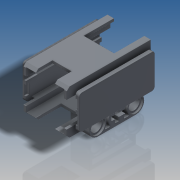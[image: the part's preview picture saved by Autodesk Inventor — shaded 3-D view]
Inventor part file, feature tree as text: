
AUTODESK INVENTOR PART (.ipt)
format: ipt  version: 2016 SP2 (Build 200236200, 236)  size: 773,632 bytes
history: native  units: in
note: dims shown in document units (in); Inventor stores cm internally (conversion verified against a paired STEP export)
features: extrude x13, sketch x3, projected_geometry x2, mirror x1, fillet x1
ambient origin geometry x8: Origin, YZ Plane, XZ Plane, XY Plane, X Axis, Y Axis, Z Axis, Center Point
bodies: Solid1 (feature_tree)
feature tree (20):
  sketch  "Sketch2"  dims[d0=0.0472in d1=1.4016in]
  extrude  "Extrusion1"  Depth=0.0472in
  extrude  "Extrusion2"  Depth=0.1732in
  extrude  "Extrusion3"  Depth=0.2835in
  extrude  "Extrusion4"  Depth=0.0157in
  extrude  "Extrusion6"  Depth=0.4252in
  extrude  "Extrusion7"  Depth=0.0157in
  extrude  "Extrusion8"  Depth=0.0157in TaperAngle=0.0deg
  extrude  "Extrusion9"  Depth=0.6299in
  extrude  "Extrusion10"  TaperAngle=0.0deg  [1 undecoded]
  extrude  "Extrusion11"  Depth=0.315in
  extrude  "Extrusion12"  TaperAngle=0.0deg  [1 undecoded]
  sketch  "Sketch4"  dims[d4=0.1417in d5=0.2835in d6=0.5039in d7=0.4252in d8=0.7244in d9=0.7244in d10=0.0in d11=0.6299in d12=0.0in d13=0.315in d14=0.0in d15=0.5039in d16=0.0in d19=0.315in d20=0.189in d21=0.2441in d22=45.0deg d23=0.2835in d24=0.2835in d25=0.0472in d26=0.063in d27=0.6772in d28=0.0787in d29=0.0472in d30=0.315in d31=0.0472in d32=0.0472in d33=0.1732in d34=0.126in d35=0.189in d36=0.0in d37=0.063in d38=0.0in d39=0.252in d40=0.0in d41=0.315in d42=0.0in d43=0.189in d44=0.0in d45=0.0472in d46=0.063in d47=0.0in d49=0.0472in d50=1.0709in d51=0.1417in d52=0.0472in d53=0.0in d54=0.0472in d55=0.5669in d56=1.2598in d57=0.0472in d58=0.1575in d59=0.7087in d60=0.2677in d61=0.1575in d62=0.0472in d63=0.0472in d64=0.063in d65=0.0in d66=0.0315in d67=0.0in d68=0.0039in d69=0.0157in]
  extrude  "Extrusion13"  Depth=0.0157in TaperAngle=0.0deg
  extrude  "Extrusion14"  Depth=0.315in
  mirror  "Mirror1"
  fillet  "Fillet1"  Radius=0.189in
  sketch  "Sketch3"  dims[d2=0.1732in d3=0.7402in]
  projected_geometry  "Projected Loop1"
  projected_geometry  "Projected Loop2"
note: 2 required parameter values undecoded (feature->parameter linkage not recoverable at this tier; creation-order binding heuristic only, values carry confidence <= 0.55)
